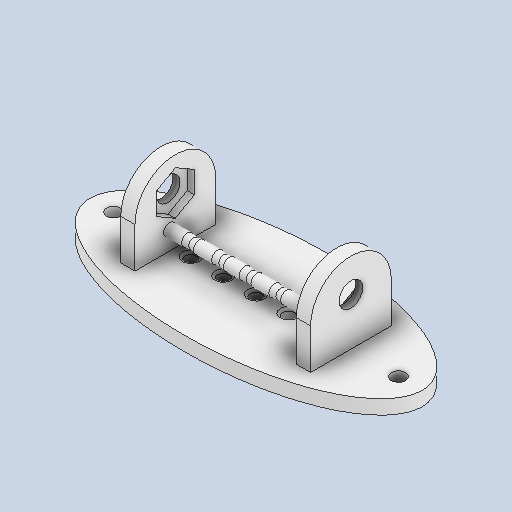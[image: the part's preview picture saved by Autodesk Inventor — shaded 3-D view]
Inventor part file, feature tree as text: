
AUTODESK INVENTOR PART (.ipt)
format: ipt  version: 2022 (Build 260153000, 153)  size: 286,208 bytes
history: native  units: in
note: dims shown in document units (in); Inventor stores cm internally (conversion verified against a paired STEP export)
features: sketch x12, extrude x11, chamfer x10, fillet x3, thread x2, hole x1
ambient origin geometry x8: Origin, YZ Plane, XZ Plane, XY Plane, X Axis, Y Axis, Z Axis, Center Point
bodies: Solid1 (feature_tree)
feature tree (39):
  extrude  "Extrusion1"  Depth=0.6693in TaperAngle=0.0deg
  extrude  "Extrusion3"  Depth=0.3346in
  fillet  "Fillet3"  Radius=0.0787in
  hole  "Hole3"  [1 undecoded]
  extrude  "Extrusion4"  Depth=0.1181in
  fillet  "Fillet4"  Radius=0.1181in
  fillet  "Fillet5"  Radius=0.1181in
  extrude  "Extrusion17"  Depth=0.0492in TaperAngle=45.0deg
  thread  "Thread1"  [1 undecoded]
  extrude  "Extrusion18"  Depth=0.0492in TaperAngle=0.0deg
  thread  "Thread2"  [1 undecoded]
  sketch  "Sketch1"  dims[d6=0.1181in d7=0.0in d22=0.6693in d23=0.0in]
  sketch  "Sketch3"  dims[d24=0.3346in d41=0.1969in d42=0.0787in]
  sketch  "Sketch6"  dims[d43=0.1969in d44=0.2362in d45=0.1575in d46=0.0787in d47=90.0deg d48=1.5748in d49=0.0in d53=1.1811in]
  sketch  "Sketch7"  dims[d54=2.3622in d55=0.1181in d56=0.1181in d57=0.1181in d58=0.0in]
  sketch  "Sketch21"  dims[d166=0.0197in]
  sketch  "Sketch22"  dims[d167=0.0197in d168=2.7559in d169=0.5906in d171=0.0591in d172=0.0in d173=0.2953in d174=0.0in d176=0.0591in d177=0.0in d178=0.2953in d179=0.0in d180=0.1819in d181=0.1819in]
  sketch  "Sketch15"  dims[d106=0.0in d107=0.1743in d108=45.0deg d109=0.0492in d110=0.0098in d112=0.0in d113=0.2417in]
  sketch  "Sketch16"  dims[d114=45.0deg d115=0.0492in d116=0.0098in d118=0.0in d119=0.2465in d120=45.0deg d121=0.0492in d122=0.0098in]
  sketch  "Sketch17"  dims[d123=45.0deg d124=0.0098in d125=0.0492in d126=45.0deg d127=0.0098in d128=0.0492in d130=0.0in d131=0.228in]
  sketch  "Sketch18"  dims[d132=45.0deg d133=0.0098in d134=0.0492in d135=45.0deg d136=0.0492in d137=0.0098in d139=0.0in d140=0.2494in]
  sketch  "Sketch19"  dims[d141=45.0deg d142=0.0492in d143=0.0098in d144=45.0deg d145=0.0098in d146=0.0492in d148=0.0in d149=0.1987in d150=45.0deg d151=0.0098in d152=0.0492in]
  sketch  "Sketch20"  dims[d158=0.0492in]
  extrude  "Extrusion11"  Depth=0.0492in TaperAngle=45.0deg
  chamfer  "Chamfer11"  Distance=0.228in
  extrude  "Extrusion12"  Depth=0.0492in TaperAngle=45.0deg
  chamfer  "Chamfer12"  Distance=0.2494in
  extrude  "Extrusion13"  Depth=0.0492in TaperAngle=45.0deg
  chamfer  "Chamfer13"  Distance=0.1987in
  chamfer  "Chamfer14"  Distance=0.0492in Angle=45.0deg
  chamfer  "Chamfer15"  Distance=2.7559in
  extrude  "Extrusion14"  Depth=0.0591in
  chamfer  "Chamfer16"  Distance=0.0591in
  chamfer  "Chamfer17"  Distance=0.2953in
  extrude  "Extrusion15"  Depth=0.0591in TaperAngle=0.0deg
  chamfer  "Chamfer18"  Distance=0.2953in
  chamfer  "Chamfer19"  Distance=0.1819in
  extrude  "Extrusion16"  Depth=0.0591in
  chamfer  "Chamfer20"  [1 undecoded]
note: 4 required parameter values undecoded (feature->parameter linkage not recoverable at this tier; creation-order binding heuristic only, values carry confidence <= 0.55)
